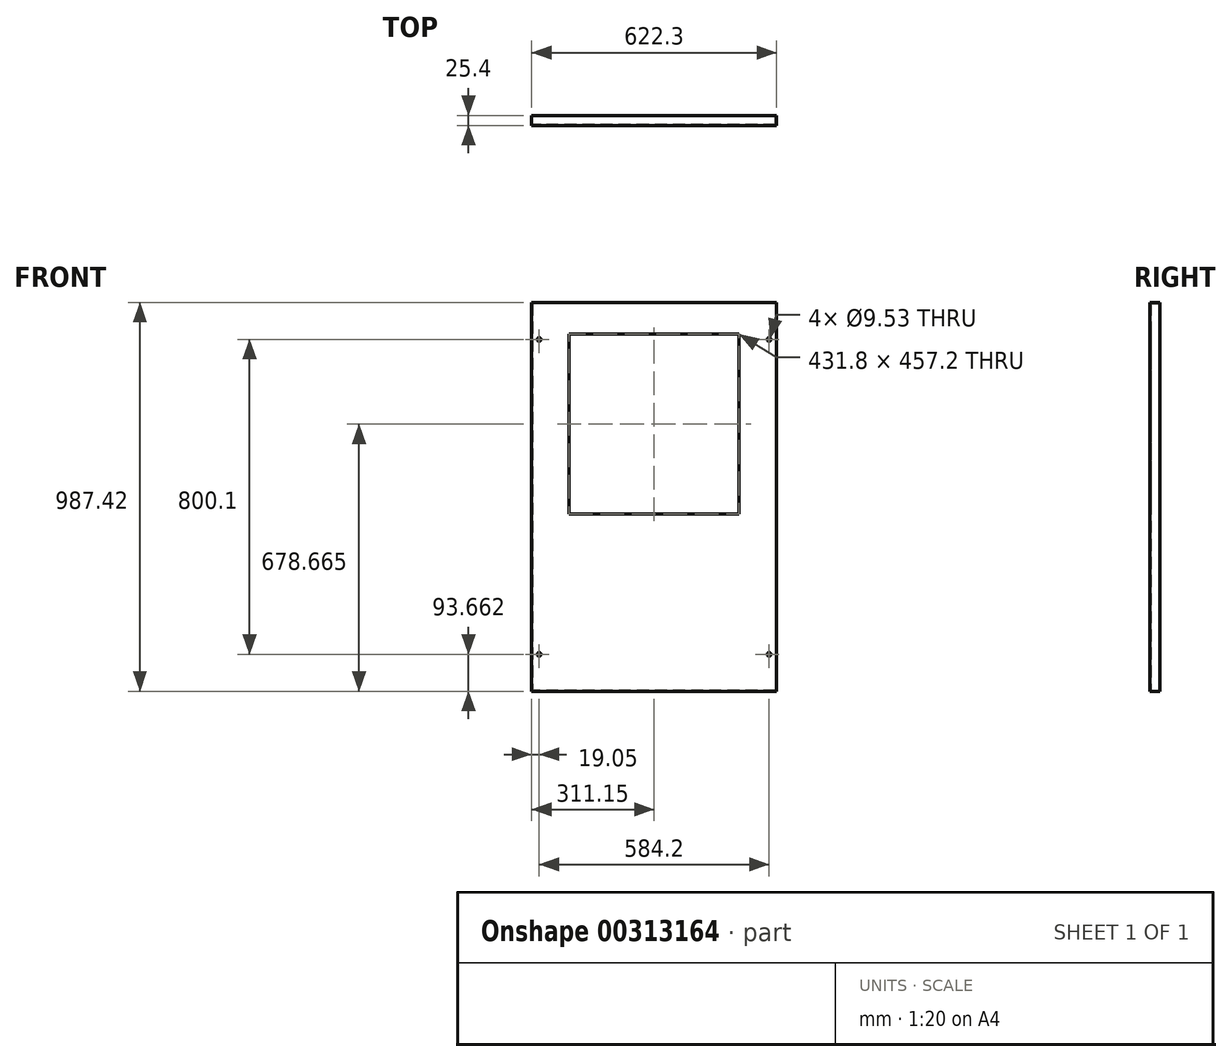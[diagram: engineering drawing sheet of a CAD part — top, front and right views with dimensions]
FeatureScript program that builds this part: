
annotation { "Feature Type Name" : "Feature", "Feature Type Description" : "" }
export const myFeature = defineFeature(function(context is Context, id is Id, definition is map)
    precondition{}
    {
        {
            var Q0;
            Q0=qCreatedBy(makeId("Front.planeOp"),FACE);
            var sketch = newSketch(context, id + "F0", { "sketchPlane" : qUnion([Q0])});
            skLineSegment(sketch, "E0.bottom", {"start": v(311.15, 987.42) * mm, "end": v(-311.15, 987.42) * mm});
            skLineSegment(sketch, "E0.top", {"start": v(311.15, 0) * mm, "end": v(-311.15, 0) * mm});
            skLineSegment(sketch, "E0.left", {"start": v(311.15, 987.43) * mm, "end": v(311.15, 0) * mm});
            skLineSegment(sketch, "E0.right", {"start": v(-311.15, 987.42) * mm, "end": v(-311.15, 0) * mm});
            skCircle(sketch, "E1", {"center": v(-292.1, 893.76) * mm, "radius": 4.76 * mm});
            skCircle(sketch, "E2", {"center": v(292.1, 893.76) * mm, "radius": 4.76 * mm});
            skCircle(sketch, "E3", {"center": v(292.1, 93.66) * mm, "radius": 4.76 * mm});
            skCircle(sketch, "E4", {"center": v(-292.1, 93.66) * mm, "radius": 4.76 * mm});
            skLineSegment(sketch, "E5.bottom", {"start": v(215.9, 907.27) * mm, "end": v(-215.9, 907.27) * mm});
            skLineSegment(sketch, "E5.top", {"start": v(215.9, 450.07) * mm, "end": v(-215.9, 450.07) * mm});
            skLineSegment(sketch, "E5.left", {"start": v(215.9, 907.27) * mm, "end": v(215.9, 450.07) * mm});
            skLineSegment(sketch, "E5.right", {"start": v(-215.9, 907.27) * mm, "end": v(-215.9, 450.07) * mm});
            skPoint(sketch, "E5.middle", {"position": v(0, 678.67) * mm});
            skPoint(sketch, "E5.middle.positionSnap0", {"position": v(0, 0) * mm});
            skPoint(sketch, "E5.centerSnap0", {"position": v(0, 0) * mm});
            skSolve(sketch);
        }
        {
            var Q0;
            Q0=qSketchRegion(id+"F0",true);
            extrude(context, id + "F1", {"entities" : qUnion([Q0]), "depth" : 25.4 * mm});
        }
        {
            var Q0;
            Q0=makeQuery(id+"F1.opExtrude","CAP_FACE",FACE,{"disambiguationData":[OSD([sQuery(id+"F0.wireOp",EDGE,"E0.bottom"),sQuery(id+"F0.wireOp",EDGE,"E0.top"),sQuery(id+"F0.wireOp",EDGE,"E0.left"),sQuery(id+"F0.wireOp",EDGE,"E0.right"),sQuery(id+"F0.wireOp",EDGE,"DnOeYdpL-yZhG-pMPP-nWlj-HbxDlVvFq81o.bottom"),sQuery(id+"F0.wireOp",EDGE,"DnOeYdpL-yZhG-pMPP-nWlj-HbxDlVvFq81o.top"),sQuery(id+"F0.wireOp",EDGE,"DnOeYdpL-yZhG-pMPP-nWlj-HbxDlVvFq81o.left"),sQuery(id+"F0.wireOp",EDGE,"DnOeYdpL-yZhG-pMPP-nWlj-HbxDlVvFq81o.right"),sQuery(id+"F0.wireOp",EDGE,"xDgMzqlZ-3YCT-1KnM-qA8u-792qYw5lw1JS"),sQuery(id+"F0.wireOp",EDGE,"Mpdr3xRK-0yTI-dkfT-nTdE-cEWg6RnXpa9N"),sQuery(id+"F0.wireOp",EDGE,"UzSud16w-tGWN-ZEeO-kTY7-zgmRVJxoJOe7"),sQuery(id+"F0.wireOp",EDGE,"QdRWkNVw-568D-XgAy-SO4V-4Q89nbcZrelq"),sQuery(id+"F0.wireOp",EDGE,"8aFPr5qc-bRuC-cZr7-87dc-hIFrfZXMsOHR"),sQuery(id+"F0.wireOp",EDGE,"mJVcAo0T-mOHa-Qb8O-DeX9-rnRp2EFAdPQ3"),sQuery(id+"F0.wireOp",EDGE,"58VjJvAl-gczf-lvPp-maZi-m7BX2DlegteS"),sQuery(id+"F0.wireOp",EDGE,"xgLxJu9m-eS83-UV5U-zqJ0-FrWtQ9vBuum0"),sQuery(id+"F0.wireOp",EDGE,"wqzXiebe-RaGP-8YjT-blUU-62aUiCvM27mv"),sQuery(id+"F0.wireOp",EDGE,"zmVhXP7j-02Ai-JLcr-0Ks7-3LBVpZUHfUrI"),sQuery(id+"F0.wireOp",EDGE,"BW3LuwXz-W35X-CTuh-aFvS-jlk6UlRIqyyT"),sQuery(id+"F0.wireOp",EDGE,"GNJOQj1j-LiCZ-vYCN-EfaB-cui9jyFQZn0N"),sQuery(id+"F0.wireOp",EDGE,"da7037a2-8101-4e2d-bd9b-c90a86b3fb6c.1.0.1"),sQuery(id+"F0.wireOp",EDGE,"da7037a2-8101-4e2d-bd9b-c90a86b3fb6c.1.0.2"),sQuery(id+"F0.wireOp",EDGE,"da7037a2-8101-4e2d-bd9b-c90a86b3fb6c.1.0.3"),sQuery(id+"F0.wireOp",EDGE,"da7037a2-8101-4e2d-bd9b-c90a86b3fb6c.1.0.4"),sQuery(id+"F0.wireOp",EDGE,"da7037a2-8101-4e2d-bd9b-c90a86b3fb6c.1.0.5"),sQuery(id+"F0.wireOp",EDGE,"da7037a2-8101-4e2d-bd9b-c90a86b3fb6c.1.0.6"),sQuery(id+"F0.wireOp",EDGE,"da7037a2-8101-4e2d-bd9b-c90a86b3fb6c.1.0.7"),sQuery(id+"F0.wireOp",EDGE,"da7037a2-8101-4e2d-bd9b-c90a86b3fb6c.1.0.8"),sQuery(id+"F0.wireOp",EDGE,"da7037a2-8101-4e2d-bd9b-c90a86b3fb6c.1.0.9"),sQuery(id+"F0.wireOp",EDGE,"da7037a2-8101-4e2d-bd9b-c90a86b3fb6c.1.0.10"),sQuery(id+"F0.wireOp",EDGE,"da7037a2-8101-4e2d-bd9b-c90a86b3fb6c.1.0.11"),sQuery(id+"F0.wireOp",EDGE,"da7037a2-8101-4e2d-bd9b-c90a86b3fb6c.1.0.12"),sQuery(id+"F0.wireOp",EDGE,"da7037a2-8101-4e2d-bd9b-c90a86b3fb6c.1.0.13"),sQuery(id+"F0.wireOp",EDGE,"da7037a2-8101-4e2d-bd9b-c90a86b3fb6c.1.0.14"),sQuery(id+"F0.wireOp",EDGE,"da7037a2-8101-4e2d-bd9b-c90a86b3fb6c.1.0.15"),sQuery(id+"F0.wireOp",EDGE,"da7037a2-8101-4e2d-bd9b-c90a86b3fb6c.1.0.16")])],"isStart":true});
            shell(context, id + "F2", {"entities" : qUnion([Q0]), "thickness" : 2.54 * mm});
        }
        {
            var Q0;
            Q0=makeQuery(id+"F2.opShell","OFFSET_FACE",FACE,{"disambiguationData":[OSD([sQuery(id+"F0.wireOp",EDGE,"E0.top")])]});
            var sketch = newSketch(context, id + "F3", { "sketchPlane" : qUnion([Q0])});
            skLineSegment(sketch, "E6.bottom", {"start": v(308.61, 0) * mm, "end": v(-308.6, 0) * mm});
            skLineSegment(sketch, "E6.top", {"start": v(308.61, -22.86) * mm, "end": v(-308.6, -22.86) * mm});
            skLineSegment(sketch, "E6.left", {"start": v(308.61, 0) * mm, "end": v(308.61, -22.86) * mm});
            skLineSegment(sketch, "E6.right", {"start": v(-308.6, 0) * mm, "end": v(-308.6, -22.86) * mm});
            skSolve(sketch);
        }
        {
            var Q0;
            Q0 = qSketchRegion(id + "F3", true);
            var Q1;
            Q1=makeQuery(id+"F2.opShell","OFFSET_FACE",FACE,{"disambiguationData":[OSD([sQuery(id+"F0.wireOp",EDGE,"E0.bottom")])]});
            extrude(context, id + "F4", {"entities" : qUnion([Q0]), "operationType" : NewBodyOperationType.REMOVE, "endBound" : BoundingType.UP_TO_SURFACE, "endBoundEntityFace" : qUnion([Q1]), "depth" : 25.4 * mm});
        }
    });
